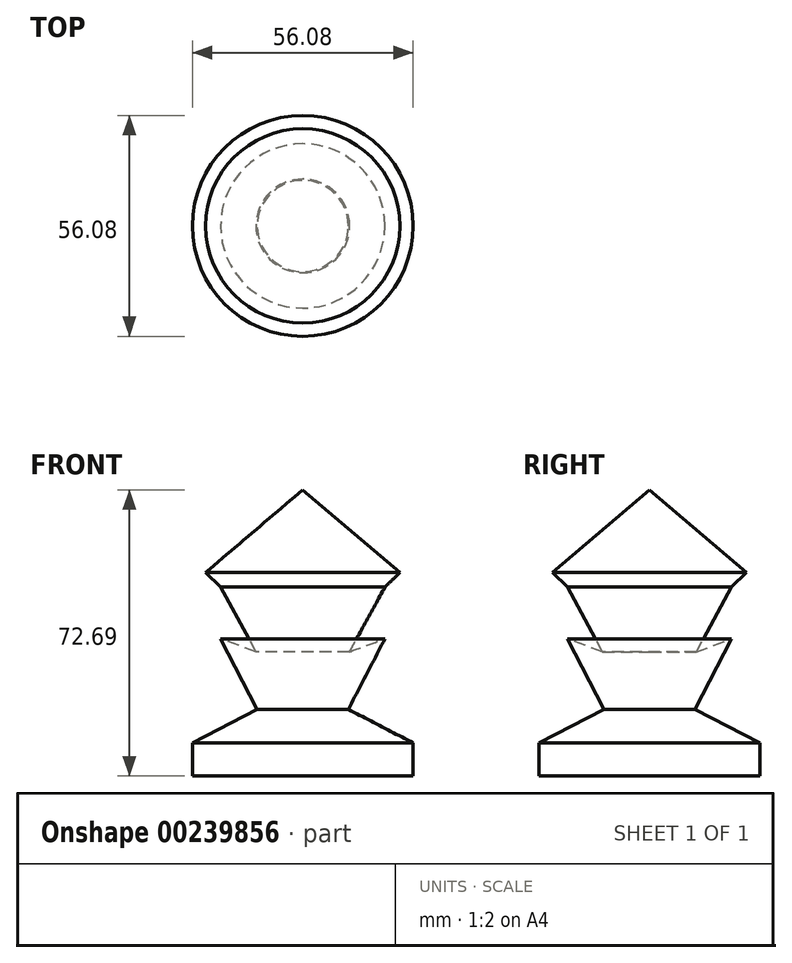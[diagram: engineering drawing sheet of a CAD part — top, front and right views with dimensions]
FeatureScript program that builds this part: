
annotation { "Feature Type Name" : "Feature", "Feature Type Description" : "" }
export const myFeature = defineFeature(function(context is Context, id is Id, definition is map)
    precondition{}
    {
        {
            var Q0;
            Q0=qCreatedBy(makeId("Front.planeOp"),FACE);
            var sketch = newSketch(context, id + "F0", { "sketchPlane" : qUnion([Q0])});
            skLineSegment(sketch, "E0", {"start": v(0, 0) * mm, "end": v(-28.04, 0) * mm});
            skLineSegment(sketch, "E1", {"start": v(-28.04, 0) * mm, "end": v(-28.04, 8.38) * mm});
            skLineSegment(sketch, "E2", {"start": v(-28.04, 8.38) * mm, "end": v(-11.58, 16.92) * mm});
            skLineSegment(sketch, "E3", {"start": v(-11.58, 16.92) * mm, "end": v(-20.87, 34.83) * mm});
            skLineSegment(sketch, "E4", {"start": v(-20.87, 34.83) * mm, "end": v(-11.89, 31.55) * mm});
            skLineSegment(sketch, "E5", {"start": v(-11.89, 31.55) * mm, "end": v(-20.87, 48) * mm});
            skLineSegment(sketch, "E6", {"start": v(-20.87, 48) * mm, "end": v(-24.69, 51.66) * mm});
            skLineSegment(sketch, "E7", {"start": v(-24.69, 51.66) * mm, "end": v(0, 72.7) * mm});
            skLineSegment(sketch, "E8", {"start": v(0, 72.7) * mm, "end": v(0, 0) * mm});
            skSolve(sketch);
        }
        {
            var Q0;
            Q0=makeQuery(id+"F0.imprint","IMPRINT",FACE,{"disambiguationData":[TD([[makeQuery(id+"F0.imprint","IMPRINT",EDGE,{"derivedFrom":sQuery(id+"F0.wireOp",EDGE,"E0")}),-1.0]])]});
            var Q1;
            Q1=sQuery(id+"F0.wireOp",EDGE,"E8");
            revolve(context, id + "F1", {"entities" : qUnion([Q0]), "axis" : qUnion([Q1]), "revolveType" : RevolveType.FULL});
        }
    });
